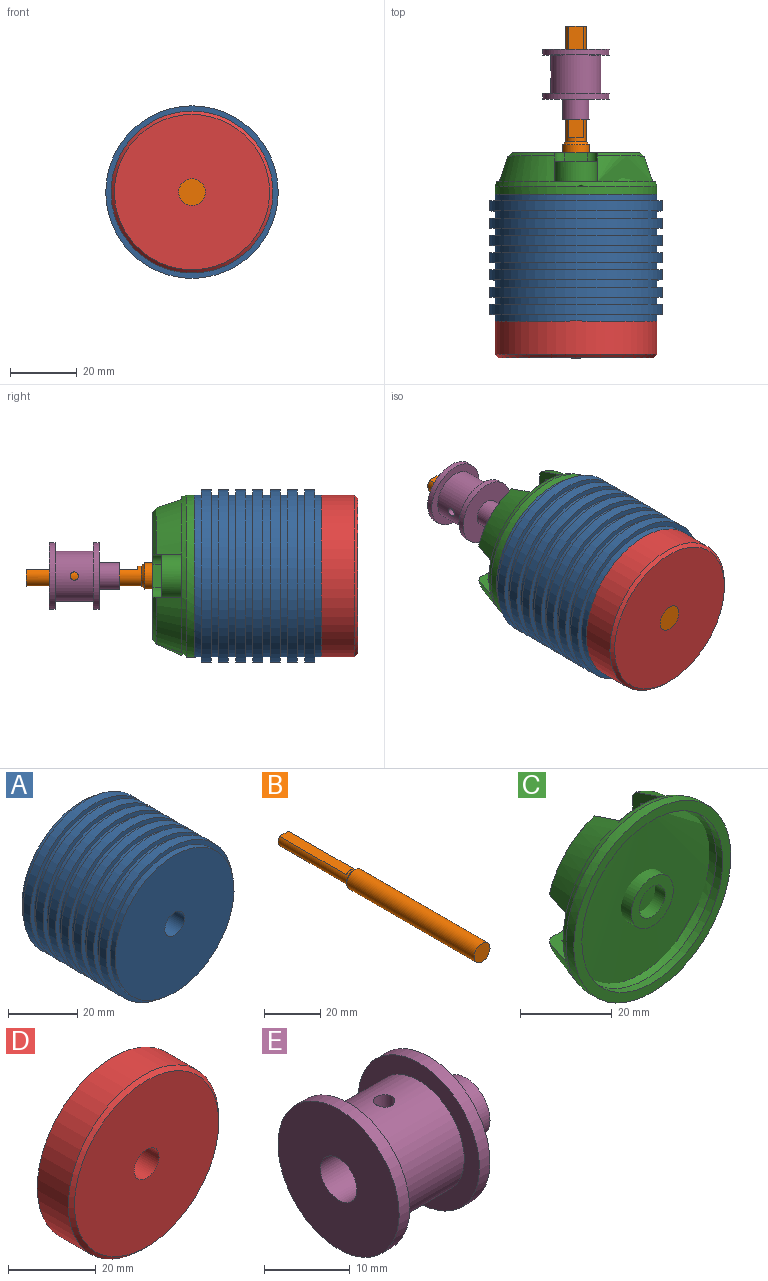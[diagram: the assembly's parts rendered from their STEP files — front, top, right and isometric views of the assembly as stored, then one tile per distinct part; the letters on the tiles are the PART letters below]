
ASSEMBLY  parts=5 mates=4
PART A: 32 faces, bbox 51.7x38x51.7 mm
  f0: plane 51.65x51.65mm, normal (0,1,0), area 247.8mm2, adj f1,f29
  f1: cylinder r=25.82mm len=51.65mm, axis (0,1,0), area 486.8mm2, adj f0,f2
  f2: plane 51.65x51.65mm, normal (0,-1,0), area 247.8mm2, adj f1,f3
  f3: cylinder r=24.25mm len=48.5mm, axis (0,1,0), area 330.1mm2, adj f2,f4
  f4: plane 51.65x51.65mm, normal (0,1,0), area 247.8mm2, adj f3,f5
  f5: cylinder r=25.82mm len=51.65mm, axis (0,1,0), area 486.8mm2, adj f4,f6
  f6: plane 51.65x51.65mm, normal (0,-1,0), area 247.8mm2, adj f5,f7
  f7: cylinder r=24.25mm len=48.5mm, axis (0,1,0), area 330.1mm2, adj f6,f8
  f8: plane 51.65x51.65mm, normal (0,1,0), area 247.8mm2, adj f7,f9
  f9: cylinder r=25.82mm len=51.65mm, axis (0,1,0), area 486.8mm2, adj f8,f10
  f10: plane 51.65x51.65mm, normal (0,-1,0), area 247.8mm2, adj f9,f11
  f11: cylinder r=24.25mm len=48.5mm, axis (0,1,0), area 330.1mm2, adj f10,f12
  f12: plane 51.65x51.65mm, normal (0,1,0), area 247.8mm2, adj f11,f13
  f13: cylinder r=25.82mm len=51.65mm, axis (0,1,0), area 486.8mm2, adj f12,f14
  f14: plane 51.65x51.65mm, normal (0,-1,0), area 247.8mm2, adj f13,f15
  f15: cylinder r=24.25mm len=48.5mm, axis (0,1,0), area 304.7mm2, adj f14,f30
  f16: cylinder r=4mm len=38mm, axis (0,1,0), area 955mm2, adj f30,f31
  f17: cylinder r=24.25mm len=48.5mm, axis (0,1,0), area 304.7mm2, adj f18,f31
  f18: plane 51.65x51.65mm, normal (0,1,0), area 247.8mm2, adj f17,f19
  f19: cylinder r=25.82mm len=51.65mm, axis (0,1,0), area 486.8mm2, adj f18,f20
  f20: plane 51.65x51.65mm, normal (0,-1,0), area 247.8mm2, adj f19,f21
  f21: cylinder r=24.25mm len=48.5mm, axis (0,1,0), area 330.1mm2, adj f20,f22
  f22: plane 51.65x51.65mm, normal (0,1,0), area 247.8mm2, adj f21,f23
  f23: cylinder r=25.82mm len=51.65mm, axis (0,1,0), area 486.8mm2, adj f22,f24
  f24: plane 51.65x51.65mm, normal (0,-1,0), area 247.8mm2, adj f23,f25
  f25: cylinder r=24.25mm len=48.5mm, axis (0,1,0), area 330.1mm2, adj f24,f26
  f26: plane 51.65x51.65mm, normal (0,1,0), area 247.8mm2, adj f25,f27
  f27: cylinder r=25.82mm len=51.65mm, axis (0,1,0), area 486.8mm2, adj f26,f28
  f28: plane 51.65x51.65mm, normal (0,-1,0), area 247.8mm2, adj f27,f29
  f29: cylinder r=24.25mm len=48.5mm, axis (0,1,0), area 330.1mm2, adj f0,f28
  f30: plane 48.5x48.5mm, normal (0,-1,0), area 1797.2mm2, adj f15,f16
  f31: plane 48.5x48.5mm, normal (0,1,0), area 1797.2mm2, adj f16,f17
PART B: 7 faces, bbox 8x99.4x8 mm
  f0: plane 6x5mm, normal (0,1,0), area 25.2mm2, adj f1,f5
  f1: cylinder r=3mm len=34.5mm, axis (0,1,0), area 481.3mm2, adj f0,f2,f5,f6
  f2: cone r=4mm half-angle=45deg, axis (0,-1,0), area 31.1mm2, adj f1,f3
  f3: cylinder r=4mm len=63.9mm, axis (0,1,0), area 1606mm2, adj f2,f4
  f4: plane 8x8mm, normal (0,-1,0), area 50.3mm2, adj f3
  f5: plane 33.5x4.47mm, normal (0,0,1), area 149.8mm2, adj f0,f1,f6
  f6: plane 4.47x1mm, normal (0,1,0), area 3.1mm2, adj f1,f5
PART C: 42 faces, bbox 48.5x12.4x48.5 mm
  f0: cone r=24.25mm half-angle=17.7deg, axis (0,-1,0), area 1147.4mm2, adj f6,f10,f11,f13,f17,f18,f20,f24
  f1: plane 38.04x38.04mm, normal (0,1,0), area 820mm2, adj f7,f11,f12,f13,f14,f15,f16,f18
  f2: cone r=21.87mm half-angle=17.7deg, axis (0,-1,0), area 729.4mm2, adj f3,f8,f10,f11,f13,f17,f18,f20
  f3: plane 36.29x36.29mm, normal (0,-1,0), area 678.5mm2, adj f2,f9,f11,f12,f13,f14,f15,f16
  f4: plane 48.5x48.5mm, normal (0,-1,0), area 361.3mm2, adj f6,f8
  f5: plane 13x13mm, normal (0,-1,0), area 82.5mm2, adj f7,f9
  f6: cylinder r=24.25mm len=48.5mm, axis (0,1,0), area 365.7mm2, adj f0,f4
  f7: cylinder r=4mm len=12.4mm, axis (0,1,0), area 311.6mm2, adj f1,f5
  f8: cylinder r=21.75mm len=43.5mm, axis (0,1,0), area 274.7mm2, adj f2,f4
  f9: cylinder r=6.5mm len=13mm, axis (0,1,0), area 404.3mm2, adj f3,f5
  f10: plane 12.7x3.6mm, normal (0,1,0), area 33.8mm2, adj f0,f2,f11,f13
  f11: plane 8.74x7.66mm, normal (0,0,-1), area 29.4mm2, adj f0,f1,f2,f3,f10,f16,f38
  f12: plane 6.7x2.5mm, normal (-1,0,0), area 16.7mm2, adj f1,f3,f15,f16
  f13: plane 8.74x7.66mm, normal (0,0,1), area 29.4mm2, adj f0,f1,f2,f3,f10,f15,f39
  f14: cylinder r=1.65mm len=3.3mm, axis (0,1,0), area 25.9mm2, adj f1,f3
  f15: cylinder r=3mm len=3mm, axis (0,-1,0), area 11.8mm2, adj f1,f3,f12,f13
  f16: cylinder r=3mm len=3mm, axis (0,1,0), area 11.8mm2, adj f1,f3,f11,f12
  f17: plane 12.7x3.6mm, normal (0,1,0), area 33.8mm2, adj f0,f2,f18,f20
  f18: plane 8.74x7.66mm, normal (-1,0,0), area 29.4mm2, adj f0,f1,f2,f3,f17,f23,f41
  f19: plane 6.7x2.5mm, normal (0,0,1), area 16.7mm2, adj f1,f3,f22,f23
  f20: plane 8.74x7.66mm, normal (1,0,0), area 29.4mm2, adj f0,f1,f2,f3,f17,f22,f38
  f21: cylinder r=1.65mm len=3.3mm, axis (0,1,0), area 25.9mm2, adj f1,f3
  f22: cylinder r=3mm len=3mm, axis (0,-1,0), area 11.8mm2, adj f1,f3,f19,f20
  f23: cylinder r=3mm len=3mm, axis (0,1,0), area 11.8mm2, adj f1,f3,f18,f19
  f24: plane 12.7x3.6mm, normal (0,1,0), area 33.8mm2, adj f0,f2,f25,f27
  f25: plane 8.74x7.66mm, normal (0,0,1), area 29.4mm2, adj f0,f1,f2,f3,f24,f30,f40
  f26: plane 6.7x2.5mm, normal (1,0,0), area 16.7mm2, adj f1,f3,f29,f30
  f27: plane 8.74x7.66mm, normal (0,0,-1), area 29.4mm2, adj f0,f1,f2,f3,f24,f29,f41
  f28: cylinder r=1.65mm len=3.3mm, axis (0,1,0), area 25.9mm2, adj f1,f3
  f29: cylinder r=3mm len=3mm, axis (0,-1,0), area 11.8mm2, adj f1,f3,f26,f27
  f30: cylinder r=3mm len=3mm, axis (0,1,0), area 11.8mm2, adj f1,f3,f25,f26
  f31: plane 47.67x47.67mm, normal (0,1,0), area 1750.8mm2, adj f0,f2,f32,f34
  f32: plane 8.74x7.66mm, normal (1,0,0), area 29.4mm2, adj f0,f1,f2,f3,f31,f37,f39
  f33: plane 6.7x2.5mm, normal (0,0,-1), area 16.7mm2, adj f1,f3,f36,f37
  f34: plane 8.74x7.66mm, normal (-1,0,0), area 29.4mm2, adj f0,f1,f2,f3,f31,f36,f40
  f35: cylinder r=1.65mm len=3.3mm, axis (0,1,0), area 25.9mm2, adj f1,f3
  f36: cylinder r=3mm len=3mm, axis (0,-1,0), area 11.8mm2, adj f1,f3,f33,f34
  f37: cylinder r=3mm len=3mm, axis (0,1,0), area 11.8mm2, adj f1,f3,f32,f33
  f38: cone r=20.05mm half-angle=53.9deg, axis (0,-1,0), area 31.7mm2, adj f0,f1,f11,f20
  f39: cone r=20.05mm half-angle=53.9deg, axis (0,-1,0), area 31.7mm2, adj f0,f1,f13,f32
  f40: cone r=20.05mm half-angle=53.9deg, axis (0,-1,0), area 31.7mm2, adj f0,f1,f25,f34
  f41: cone r=20.05mm half-angle=53.9deg, axis (0,-1,0), area 31.7mm2, adj f0,f1,f18,f27
PART D: 5 faces, bbox 48.5x11x48.5 mm
  f0: plane 48.5x48.5mm, normal (0,1,0), area 1797.2mm2, adj f1,f3
  f1: cylinder r=24.25mm len=48.5mm, axis (0,1,0), area 1523.7mm2, adj f0,f4
  f2: plane 46.5x46.5mm, normal (0,-1,0), area 1648mm2, adj f3,f4
  f3: cylinder r=4mm len=11mm, axis (0,1,0), area 276.5mm2, adj f0,f2
  f4: cone r=24.25mm half-angle=45deg, axis (0,1,0), area 211mm2, adj f1,f2
PART E: 11 faces, bbox 21x20x20 mm
  f0: cylinder r=7.5mm len=15mm, axis (-1,0,0), area 537mm2, adj f6,f7,f10
  f1: cylinder r=3mm len=21mm, axis (-1,0,0), area 390.8mm2, adj f2,f9,f10
  f2: plane 8x8mm, normal (1,0,0), area 22mm2, adj f1,f3
  f3: cylinder r=4mm len=8mm, axis (-1,0,0), area 150.8mm2, adj f2,f4
  f4: plane 20x20mm, normal (1,0,0), area 263.9mm2, adj f3,f5
  f5: cylinder r=10mm len=20mm, axis (-1,0,0), area 110mm2, adj f4,f6
  f6: plane 20x20mm, normal (-1,0,0), area 137.4mm2, adj f0,f5
  f7: plane 20x20mm, normal (1,0,0), area 137.4mm2, adj f0,f8
  f8: cylinder r=10mm len=20mm, axis (-1,0,0), area 110mm2, adj f7,f9
  f9: plane 20x20mm, normal (-1,0,0), area 285.9mm2, adj f1,f8
  f10: cylinder r=1.25mm len=4.77mm, axis (0,0,1), area 36mm2, adj f0,f1
PLACE A t=(26.84,6.28,45.23)mm
PLACE B t=(26.84,6.28,45.23)mm
PLACE C t=(26.84,6.28,45.23)mm
PLACE D t=(26.84,6.28,45.23)mm
PLACE E rot(axis=(0.58,-0.58,-0.58),120deg) t=(26.84,29.83,45.23)mm
MATE revolute B.f1 <-> D.f1  axis (0,-1,0) through (26.84,-55.12,45.23)mm
MATE slider E.f0 <-> B.f1  axis (0,1,0) through (26.84,37.33,45.23)mm
MATE fastened D.f1 <-> A.f1  axis (0,1,0) through (26.84,-44.12,45.23)mm
MATE fastened C.f0 <-> A.f1  axis (0,-1,0) through (26.84,-6.12,45.23)mm
